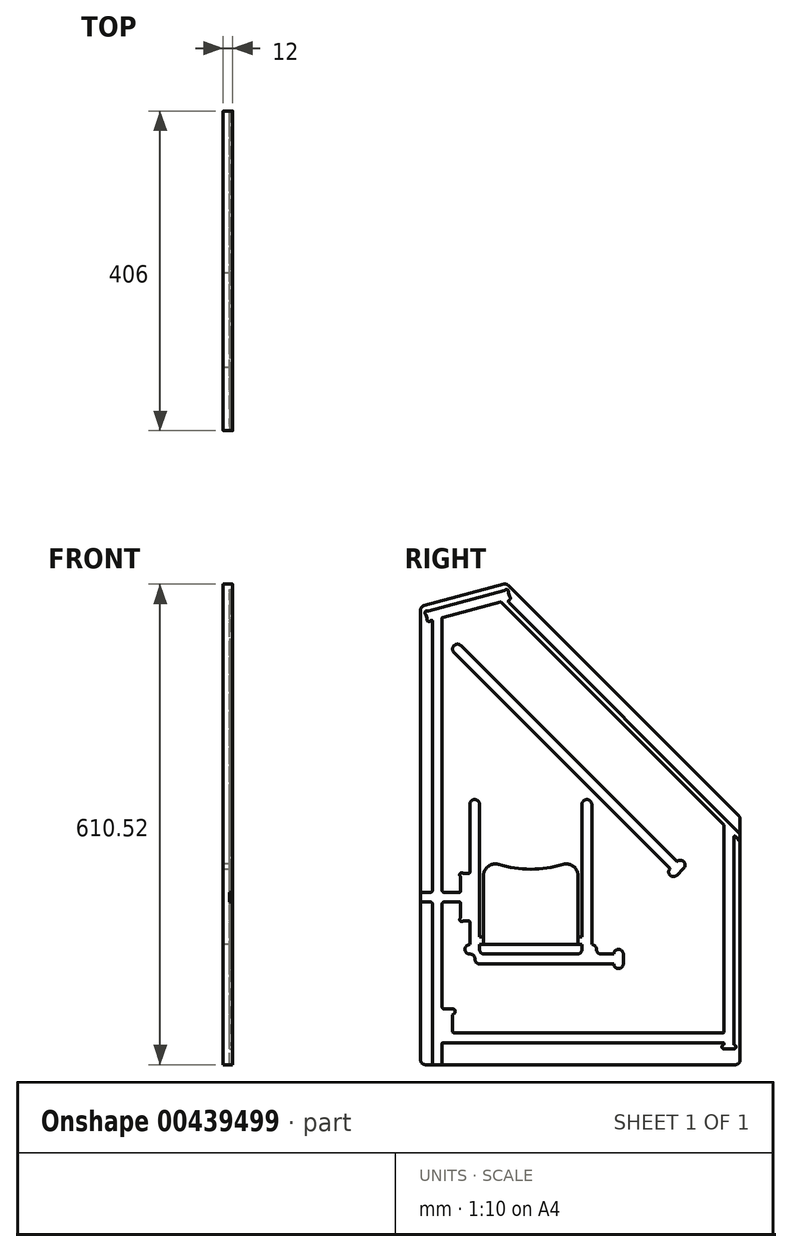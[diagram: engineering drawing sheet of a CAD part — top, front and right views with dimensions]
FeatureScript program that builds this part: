
annotation { "Feature Type Name" : "Feature", "Feature Type Description" : "" }
export const myFeature = defineFeature(function(context is Context, id is Id, definition is map)
    precondition{}
    {
        {
            var Q0;
            Q0=qCreatedBy(makeId("Right.planeOp"),FACE);
            var sketch = newSketch(context, id + "F0", { "sketchPlane" : qUnion([Q0])});
            skLineSegment(sketch, "E0", {"start": v(0, 0) * mm, "end": v(0, 582) * mm});
            skLineSegment(sketch, "E1", {"start": v(0, 582) * mm, "end": v(109.02, 611.21) * mm});
            skLineSegment(sketch, "E2", {"start": v(109.02, 611.21) * mm, "end": v(406, 314.23) * mm});
            skLineSegment(sketch, "E3", {"start": v(406, 314.23) * mm, "end": v(406, 0) * mm});
            skLineSegment(sketch, "E4", {"start": v(406, 0) * mm, "end": v(0, 0) * mm});
            skLineSegment(sketch, "E5", {"start": v(80, 240) * mm, "end": v(80, 152.5) * mm});
            skLineSegment(sketch, "E6", {"start": v(80, 152.5) * mm, "end": v(200, 152.5) * mm});
            skLineSegment(sketch, "E7", {"start": v(200, 152.5) * mm, "end": v(200, 240) * mm});
            skArc(sketch, "E8", {"start": v(200, 240) * mm, "mid": v(193.94, 252.05) * mm, "end": v(180.65, 254.35) * mm});
            skArc(sketch, "E9", {"start": v(99.35, 254.35) * mm, "mid": v(86.06, 252.05) * mm, "end": v(80, 240) * mm});
            skArc(sketch, "E10", {"start": v(99.35, 254.35) * mm, "mid": v(140, 248.32) * mm, "end": v(180.65, 254.35) * mm});
            skSolve(sketch);
        }
        {
            var Q0;
            Q0=qSketchRegion(id+"F0",true);
            extrude(context, id + "F1", {"entities" : qUnion([Q0]), "depth" : 12 * mm, "offsetDistance" : 25.4 * mm});
        }
        {
            var Q0;
            Q0=makeQuery(id+"F1.opExtrude","CAP_FACE",FACE,{"disambiguationData":[OSD([sQuery(id+"F0.wireOp",EDGE,"E0"),sQuery(id+"F0.wireOp",EDGE,"E1"),sQuery(id+"F0.wireOp",EDGE,"E2"),sQuery(id+"F0.wireOp",EDGE,"E3"),sQuery(id+"F0.wireOp",EDGE,"E4")])],"isStart":false});
            var sketch = newSketch(context, id + "F2", { "sketchPlane" : qUnion([Q0])});
            skLineSegment(sketch, "E11", {"start": v(27.5, 0) * mm, "end": v(27.5, 28) * mm});
            skLineSegment(sketch, "E12", {"start": v(27.5, 28) * mm, "end": v(385.5, 28) * mm});
            skLineSegment(sketch, "E13", {"start": v(385.5, 28) * mm, "end": v(385.5, 20) * mm});
            skLineSegment(sketch, "E14", {"start": v(385.5, 20) * mm, "end": v(398, 20) * mm});
            skLineSegment(sketch, "E15", {"start": v(398, 20) * mm, "end": v(398, 291.82) * mm});
            skLineSegment(sketch, "E16", {"start": v(398, 291.82) * mm, "end": v(406, 283.82) * mm});
            skLineSegment(sketch, "E17", {"start": v(410.6, 288.42) * mm, "end": v(109.02, 589.99) * mm});
            skLineSegment(sketch, "E18", {"start": v(101.77, 588.05) * mm, "end": v(385.5, 304.32) * mm});
            skLineSegment(sketch, "E19", {"start": v(385.5, 304.32) * mm, "end": v(385.5, 40.5) * mm});
            skLineSegment(sketch, "E20", {"start": v(385.5, 40.5) * mm, "end": v(40.5, 40.5) * mm});
            skLineSegment(sketch, "E21", {"start": v(27.5, 71) * mm, "end": v(27.5, 128) * mm});
            skLineSegment(sketch, "E22", {"start": v(27.5, 128) * mm, "end": v(257.5, 128) * mm});
            skLineSegment(sketch, "E23", {"start": v(257.5, 128) * mm, "end": v(257.5, 140.5) * mm});
            skLineSegment(sketch, "E24", {"start": v(257.5, 140.5) * mm, "end": v(27.5, 140.5) * mm});
            skLineSegment(sketch, "E25", {"start": v(27.5, 568.15) * mm, "end": v(101.77, 588.05) * mm});
            skLineSegment(sketch, "E26", {"start": v(105.79, 602.06) * mm, "end": v(9.55, 576.28) * mm});
            skLineSegment(sketch, "E27", {"start": v(27.5, 140.5) * mm, "end": v(27.5, 206.5) * mm});
            skLineSegment(sketch, "E28", {"start": v(15, 0) * mm, "end": v(15, 206.5) * mm});
            skLineSegment(sketch, "E29", {"start": v(15, 564.8) * mm, "end": v(12.79, 564.2) * mm});
            skLineSegment(sketch, "E30", {"start": v(9.24, 563.25) * mm, "end": v(8.28, 566.8) * mm, "construction": true});
            skLineSegment(sketch, "E31", {"start": v(51.4, 532.36) * mm, "end": v(334.24, 249.52) * mm});
            skLineSegment(sketch, "E32", {"start": v(334.24, 249.52) * mm, "end": v(325.4, 240.68) * mm});
            skLineSegment(sketch, "E33", {"start": v(325.4, 240.68) * mm, "end": v(42.55, 523.52) * mm});
            skLineSegment(sketch, "E34", {"start": v(406, 283.82) * mm, "end": v(410.6, 288.42) * mm});
            skLineSegment(sketch, "E35", {"start": v(105.79, 602.06) * mm, "end": v(109.02, 589.99) * mm, "construction": true});
            skLineSegment(sketch, "E36", {"start": v(109.02, 589.99) * mm, "end": v(104.43, 585.4) * mm, "construction": true});
            skLineSegment(sketch, "E37", {"start": v(205, 140.5) * mm, "end": v(205, 330.5) * mm});
            skLineSegment(sketch, "E38", {"start": v(75, 330.5) * mm, "end": v(75, 140.5) * mm});
            skLineSegment(sketch, "E39.left", {"start": v(62.5, 330.5) * mm, "end": v(62.5, 243) * mm});
            skLineSegment(sketch, "E39.right", {"start": v(217.5, 330.5) * mm, "end": v(217.5, 140.5) * mm});
            skLineSegment(sketch, "E40", {"start": v(205, 140.5) * mm, "end": v(217.5, 140.5) * mm});
            skLineSegment(sketch, "E41", {"start": v(75, 140.5) * mm, "end": v(62.5, 140.5) * mm});
            skLineSegment(sketch, "E42", {"start": v(75, 140.5) * mm, "end": v(205, 164.5) * mm, "construction": true});
            skLineSegment(sketch, "E43", {"start": v(51.4, 532.36) * mm, "end": v(42.55, 523.52) * mm, "construction": true});
            skArc(sketch, "E44", {"start": v(51.4, 532.36) * mm, "mid": v(42.55, 532.36) * mm, "end": v(42.55, 523.52) * mm});
            skLineSegment(sketch, "E45", {"start": v(62.5, 330.5) * mm, "end": v(75, 330.5) * mm, "construction": true});
            skLineSegment(sketch, "E46", {"start": v(205, 330.5) * mm, "end": v(217.5, 330.5) * mm, "construction": true});
            skArc(sketch, "E47", {"start": v(62.5, 330.5) * mm, "mid": v(68.75, 336.75) * mm, "end": v(75, 330.5) * mm});
            skArc(sketch, "E48", {"start": v(205, 330.5) * mm, "mid": v(211.25, 336.75) * mm, "end": v(217.5, 330.5) * mm});
            skLineSegment(sketch, "E49", {"start": v(27.5, 206.5) * mm, "end": v(50.5, 206.5) * mm});
            skLineSegment(sketch, "E50", {"start": v(50.5, 206.5) * mm, "end": v(50.5, 186.18) * mm});
            skLineSegment(sketch, "E51", {"start": v(50.5, 182.5) * mm, "end": v(54.18, 182.5) * mm, "construction": true});
            skLineSegment(sketch, "E52", {"start": v(50.5, 243) * mm, "end": v(54.18, 243) * mm, "construction": true});
            skLineSegment(sketch, "E53", {"start": v(27.5, 219) * mm, "end": v(50.5, 219) * mm});
            skLineSegment(sketch, "E54", {"start": v(50.5, 219) * mm, "end": v(50.5, 239.32) * mm});
            skLineSegment(sketch, "E55", {"start": v(27.5, 219) * mm, "end": v(27.5, 568.15) * mm});
            skLineSegment(sketch, "E56", {"start": v(62.5, 182.5) * mm, "end": v(62.5, 140.5) * mm});
            skLineSegment(sketch, "E57", {"start": v(15, 219) * mm, "end": v(0, 219) * mm});
            skLineSegment(sketch, "E58", {"start": v(0, 219) * mm, "end": v(0, 206.5) * mm});
            skLineSegment(sketch, "E59", {"start": v(0, 206.5) * mm, "end": v(15, 206.5) * mm});
            skLineSegment(sketch, "E60.trimOffspring", {"start": v(15, 219) * mm, "end": v(15, 564.8) * mm});
            skLineSegment(sketch, "E61", {"start": v(40.5, 40.5) * mm, "end": v(40.5, 64) * mm});
            skLineSegment(sketch, "E62", {"start": v(109.02, 589.99) * mm, "end": v(110.3, 590.33) * mm});
            skLineSegment(sketch, "E63", {"start": v(113.85, 591.28) * mm, "end": v(112.9, 594.84) * mm, "construction": true});
            skLineSegment(sketch, "E64", {"start": v(110.62, 603.36) * mm, "end": v(107.07, 602.4) * mm, "construction": true});
            skLineSegment(sketch, "E65", {"start": v(69, 140.5) * mm, "end": v(69, 128) * mm});
            skLineSegment(sketch, "E66", {"start": v(27.5, 140.5) * mm, "end": v(27.5, 128) * mm});
            skLineSegment(sketch, "E67", {"start": v(40.5, 71) * mm, "end": v(27.5, 71) * mm});
            skArc(sketch, "E68", {"start": v(40.5, 64) * mm, "mid": v(44, 67.5) * mm, "end": v(40.5, 71) * mm});
            skLineSegment(sketch, "E69", {"start": v(40.5, 64) * mm, "end": v(40.5, 71) * mm, "construction": true});
            skArc(sketch, "E70", {"start": v(8.28, 566.8) * mm, "mid": v(9.24, 563.25) * mm, "end": v(12.79, 564.2) * mm});
            skLineSegment(sketch, "E71", {"start": v(12.79, 564.2) * mm, "end": v(9.24, 563.25) * mm, "construction": true});
            skLineSegment(sketch, "E72", {"start": v(8.28, 566.8) * mm, "end": v(6.95, 571.77) * mm});
            skArc(sketch, "E73", {"start": v(9.55, 576.28) * mm, "mid": v(6, 575.33) * mm, "end": v(6.95, 571.77) * mm});
            skLineSegment(sketch, "E74", {"start": v(6.95, 571.77) * mm, "end": v(6, 575.33) * mm, "construction": true});
            skLineSegment(sketch, "E75", {"start": v(9.55, 576.28) * mm, "end": v(6, 575.33) * mm, "construction": true});
            skArc(sketch, "E76", {"start": v(111.57, 599.8) * mm, "mid": v(110.62, 603.36) * mm, "end": v(107.07, 602.4) * mm});
            skLineSegment(sketch, "E77", {"start": v(111.57, 599.8) * mm, "end": v(110.62, 603.36) * mm, "construction": true});
            skLineSegment(sketch, "E78", {"start": v(107.07, 602.4) * mm, "end": v(105.79, 602.06) * mm});
            skArc(sketch, "E79", {"start": v(110.3, 590.33) * mm, "mid": v(113.85, 591.28) * mm, "end": v(112.9, 594.84) * mm});
            skLineSegment(sketch, "E80", {"start": v(112.9, 594.84) * mm, "end": v(111.57, 599.8) * mm});
            skLineSegment(sketch, "E81", {"start": v(110.3, 590.33) * mm, "end": v(113.85, 591.28) * mm, "construction": true});
            skLineSegment(sketch, "E82", {"start": v(112.9, 594.84) * mm, "end": v(110.3, 590.33) * mm, "construction": true});
            skLineSegment(sketch, "E83", {"start": v(54.18, 243) * mm, "end": v(62.5, 243) * mm});
            skLineSegment(sketch, "E84", {"start": v(50.5, 239.32) * mm, "end": v(50.5, 243) * mm, "construction": true});
            skArc(sketch, "E85", {"start": v(54.18, 243) * mm, "mid": v(50.5, 243) * mm, "end": v(50.5, 239.32) * mm});
            skLineSegment(sketch, "E86", {"start": v(54.18, 243) * mm, "end": v(50.5, 239.32) * mm, "construction": true});
            skLineSegment(sketch, "E87", {"start": v(54.18, 182.5) * mm, "end": v(62.5, 182.5) * mm});
            skLineSegment(sketch, "E88", {"start": v(50.5, 186.18) * mm, "end": v(50.5, 182.5) * mm, "construction": true});
            skArc(sketch, "E89", {"start": v(50.5, 186.18) * mm, "mid": v(50.5, 182.5) * mm, "end": v(54.18, 182.5) * mm});
            skLineSegment(sketch, "E90", {"start": v(54.18, 182.5) * mm, "end": v(50.5, 186.18) * mm, "construction": true});
            skSolve(sketch);
        }
        {
            var Q0;
            {var subQ1=sQuery(id+"F2.wireOp",EDGE,"E11");Q0=makeQuery(id+"F2.imprint","IMPRINT",FACE,{"disambiguationData":[TD([[makeQuery(id+"F2.imprint","IMPRINT",EDGE,{"derivedFrom":subQ1}),1.0]])]});}
            var Q1;
            Q1=makeQuery(id+"F2.imprint","IMPRINT",FACE,{"disambiguationData":[TD([[makeQuery(id+"F2.imprint","IMPRINT",EDGE,{"derivedFrom":sQuery(id+"F2.wireOp",EDGE,"E37")}),-1.0]])]});
            var Q2;
            Q2=makeQuery(id+"F2.imprint","IMPRINT",FACE,{"disambiguationData":[TD([[makeQuery(id+"F2.imprint","IMPRINT",EDGE,{"derivedFrom":sQuery(id+"F2.wireOp",EDGE,"E31")}),-1.0]])]});
            var Q3;
            Q3=makeQuery(id+"F2.imprint","IMPRINT",FACE,{"disambiguationData":[TD([[makeQuery(id+"F2.imprint","IMPRINT",EDGE,{"derivedFrom":sQuery(id+"F2.wireOp",EDGE,"E38")}),-1.0]])]});
            var Q4;
            {var subQ0=sQuery(id+"F2.wireOp",EDGE,"E23");Q4=makeQuery(id+"F2.imprint","IMPRINT",FACE,{"disambiguationData":[TD([[makeQuery(id+"F2.imprint","IMPRINT",EDGE,{"derivedFrom":subQ0}),1.0]])]});}
            extrude(context, id + "F3", {"entities" : qUnion([Q0, Q1, Q2, Q3, Q4]), "operationType" : NewBodyOperationType.REMOVE, "oppositeDirection" : true, "depth" : 4 * mm, "offsetDistance" : 25 * mm});
        }
        {
            var Q0;
            {var subQ0=sQuery(id+"F0.wireOp",EDGE,"E0");var subQ1=sQuery(id+"F0.wireOp",EDGE,"E4");var subQ2=sQuery(id+"F0.wireOp",EDGE,"E3");var subQ3=sQuery(id+"F0.wireOp",EDGE,"E1");var subQ4=sQuery(id+"F0.wireOp",EDGE,"E2");Q0=makeQuery(id+"F3.boolean.opBoolean","SPLIT",FACE,{"disambiguationData":[TD([makeQuery(id+"F1.opExtrude","SWEPT_FACE",FACE,{"disambiguationData":[OSD([subQ0])]})])],"derivedFrom":makeQuery(id+"F1.opExtrude","CAP_FACE",FACE,{"disambiguationData":[OSD([subQ0,subQ3,subQ4,subQ2,subQ1])],"isStart":false})});}
            var sketch = newSketch(context, id + "F4", { "sketchPlane" : qUnion([Q0])});
            skArc(sketch, "E91", {"start": v(334.24, 249.52) * mm, "mid": v(334.24, 258) * mm, "end": v(325.75, 258) * mm});
            skArc(sketch, "E92", {"start": v(316.91, 249.16) * mm, "mid": v(316.91, 240.68) * mm, "end": v(325.4, 240.68) * mm});
            skArc(sketch, "E93", {"start": v(257.5, 140.5) * mm, "mid": v(251.5, 146.5) * mm, "end": v(245.5, 140.5) * mm});
            skArc(sketch, "E94", {"start": v(245.5, 128) * mm, "mid": v(251.5, 122) * mm, "end": v(257.5, 128) * mm});
            skArc(sketch, "E95", {"start": v(385.5, 25.2) * mm, "mid": v(382.9, 22.6) * mm, "end": v(385.5, 20) * mm});
            skArc(sketch, "E96", {"start": v(398, 20) * mm, "mid": v(400.6, 22.6) * mm, "end": v(398, 25.2) * mm});
            skLineSegment(sketch, "E97", {"start": v(245.5, 140.5) * mm, "end": v(245.5, 128) * mm});
            skLineSegment(sketch, "E98", {"start": v(257.5, 140.5) * mm, "end": v(257.5, 128) * mm});
            skLineSegment(sketch, "E99", {"start": v(385.5, 20) * mm, "end": v(398, 20) * mm});
            skLineSegment(sketch, "E100", {"start": v(385.5, 25.2) * mm, "end": v(398, 25.2) * mm});
            skLineSegment(sketch, "E101", {"start": v(325.75, 258) * mm, "end": v(316.91, 249.16) * mm});
            skLineSegment(sketch, "E102", {"start": v(325.4, 240.68) * mm, "end": v(334.24, 249.52) * mm});
            skPoint(sketch, "E103", {"position": v(9.55, 576.28) * mm});
            skArc(sketch, "E104", {"start": v(62.5, 152.5) * mm, "mid": v(56.5, 146.5) * mm, "end": v(62.5, 140.5) * mm});
            skLineSegment(sketch, "E105", {"start": v(140, 154.95) * mm, "end": v(140, 133.36) * mm, "construction": true});
            skArc(sketch, "E106.MirrorCS", {"start": v(217.5, 152.5) * mm, "mid": v(223.5, 146.5) * mm, "end": v(217.5, 140.5) * mm});
            skPoint(sketch, "E107", {"position": v(50.5, 219) * mm});
            skPoint(sketch, "E108", {"position": v(50.5, 206.5) * mm});
            skLineSegment(sketch, "E109", {"start": v(62.5, 152.5) * mm, "end": v(62.5, 140.5) * mm});
            skLineSegment(sketch, "E110", {"start": v(217.5, 152.5) * mm, "end": v(217.5, 140.5) * mm});
            skSolve(sketch);
        }
        {
            var Q0;
            {var subQ0=sQuery(id+"F0.wireOp",EDGE,"E8");var subQ1=sQuery(id+"F0.wireOp",EDGE,"E7");var subQ2=sQuery(id+"F0.wireOp",EDGE,"E6");var subQ3=sQuery(id+"F0.wireOp",EDGE,"E5");var subQ4=sQuery(id+"F0.wireOp",EDGE,"E9");var subQ5=sQuery(id+"F0.wireOp",EDGE,"E10");Q0=makeQuery(id+"F3.boolean.opBoolean","SPLIT",FACE,{"disambiguationData":[TD([makeQuery(id+"F1.opExtrude","SWEPT_FACE",FACE,{"disambiguationData":[OSD([subQ3])]})])],"derivedFrom":makeQuery(id+"F1.opExtrude","CAP_FACE",FACE,{"disambiguationData":[OSD([sQuery(id+"F0.wireOp",EDGE,"E0"),sQuery(id+"F0.wireOp",EDGE,"E1"),sQuery(id+"F0.wireOp",EDGE,"E2"),sQuery(id+"F0.wireOp",EDGE,"E3"),sQuery(id+"F0.wireOp",EDGE,"E4"),subQ3,subQ2,subQ1,subQ0,subQ4,subQ5])],"isStart":false})});}
            var sketch = newSketch(context, id + "F5", { "sketchPlane" : qUnion([Q0])});
            skLineSegment(sketch, "E111", {"start": v(76.5, 162.5) * mm, "end": v(80, 162.5) * mm});
            skLineSegment(sketch, "E112", {"start": v(80, 162.5) * mm, "end": v(75, 162.5) * mm});
            skLineSegment(sketch, "E113", {"start": v(80, 152.5) * mm, "end": v(75, 152.5) * mm});
            skLineSegment(sketch, "E114", {"start": v(75, 152.5) * mm, "end": v(75, 162.5) * mm});
            skLineSegment(sketch, "E115", {"start": v(80, 162.5) * mm, "end": v(80, 152.5) * mm});
            skLineSegment(sketch, "E116", {"start": v(75, 162.5) * mm, "end": v(75, 152.5) * mm});
            skLineSegment(sketch, "E117", {"start": v(200, 162.5) * mm, "end": v(200, 152.5) * mm});
            skLineSegment(sketch, "E118", {"start": v(200, 152.5) * mm, "end": v(205, 152.5) * mm});
            skLineSegment(sketch, "E119", {"start": v(205, 152.5) * mm, "end": v(205, 162.5) * mm});
            skLineSegment(sketch, "E120", {"start": v(205, 162.5) * mm, "end": v(200, 162.5) * mm});
            skSolve(sketch);
        }
        {
            var Q0;
            Q0 = qSketchRegion(id + "F5", true);
            extrude(context, id + "F6", {"entities" : qUnion([Q0]), "operationType" : NewBodyOperationType.REMOVE, "oppositeDirection" : true, "depth" : 4 * mm, "offsetDistance" : 25 * mm});
        }
        {
            var Q0;
            Q0=qSketchRegion(id+"F4",true);
            var Q1;
            {var subQ0=sQuery(id+"F4.wireOp",EDGE,"urzTXQ1m-be9f-dkH4-n3dN-gv34R3q4TUyH");var subQ1=makeQuery(id+"F3.boolean.opBoolean","COPY",EDGE,{"derivedFrom":makeQuery(id+"F3.opExtrude","CAP_EDGE",EDGE,{"disambiguationData":[OSD([sQuery(id+"F2.wireOp",EDGE,"E26")])],"isStart":true})});var subQ3=makeQuery(id+"F4.imprint","INTERSECT",VERTEX,{"derivedFrom":[subQ1,subQ0]});Q1=makeQuery(id+"F4.imprint","IMPRINT",FACE,{"disambiguationData":[TD([[makeQuery(id+"F4.imprint","IMPRINT",EDGE,{"disambiguationData":[TD([[subQ3,-1.0]])],"derivedFrom":subQ0}),1.0]])]});}
            var Q2;
            {var subQ0=sQuery(id+"F4.wireOp",EDGE,"xMWXty8K-vTmh-I9ST-5zzS-5fXN0JypUEpW");var subQ1=makeQuery(id+"F3.boolean.opBoolean","COPY",EDGE,{"derivedFrom":makeQuery(id+"F3.opExtrude","CAP_EDGE",EDGE,{"disambiguationData":[OSD([sQuery(id+"F2.wireOp",EDGE,"E30")])],"isStart":true})});var subQ3=makeQuery(id+"F4.imprint","INTERSECT",VERTEX,{"derivedFrom":[subQ1,subQ0]});Q2=makeQuery(id+"F4.imprint","IMPRINT",FACE,{"disambiguationData":[TD([[makeQuery(id+"F4.imprint","IMPRINT",EDGE,{"disambiguationData":[TD([[subQ3,-1.0]])],"derivedFrom":subQ0}),1.0]])]});}
            var Q3;
            {var subQ0=sQuery(id+"F4.wireOp",EDGE,"xMWXty8K-vTmh-I9ST-5zzS-5fXN0JypUEpW");var subQ1=makeQuery(id+"F3.boolean.opBoolean","COPY",EDGE,{"derivedFrom":makeQuery(id+"F3.opExtrude","CAP_EDGE",EDGE,{"disambiguationData":[OSD([sQuery(id+"F2.wireOp",EDGE,"E29")])],"isStart":true})});var subQ3=makeQuery(id+"F4.imprint","INTERSECT",VERTEX,{"derivedFrom":[subQ1,subQ0]});Q3=makeQuery(id+"F4.imprint","IMPRINT",FACE,{"disambiguationData":[TD([[makeQuery(id+"F4.imprint","IMPRINT",EDGE,{"disambiguationData":[TD([[subQ3,1.0]])],"derivedFrom":subQ0}),1.0]])]});}
            var Q4;
            {var subQ0=sQuery(id+"F4.wireOp",EDGE,"urzTXQ1m-be9f-dkH4-n3dN-gv34R3q4TUyH");var subQ1=makeQuery(id+"F3.boolean.opBoolean","COPY",EDGE,{"derivedFrom":makeQuery(id+"F3.opExtrude","CAP_EDGE",EDGE,{"disambiguationData":[OSD([sQuery(id+"F2.wireOp",EDGE,"E30")])],"isStart":true})});var subQ3=makeQuery(id+"F4.imprint","INTERSECT",VERTEX,{"derivedFrom":[subQ1,subQ0]});Q4=makeQuery(id+"F4.imprint","IMPRINT",FACE,{"disambiguationData":[TD([[makeQuery(id+"F4.imprint","IMPRINT",EDGE,{"disambiguationData":[TD([[subQ3,1.0]])],"derivedFrom":subQ0}),1.0]])]});}
            var Q5;
            {var subQ0=sQuery(id+"F4.wireOp",EDGE,"6hAEF9lr-ykpB-nCDN-qJi7-kB8WBNifAdNi");Q5=makeQuery(id+"F4.imprint","IMPRINT",FACE,{"disambiguationData":[TD([[makeQuery(id+"F4.imprint","IMPRINT",EDGE,{"derivedFrom":subQ0}),1.0]])]});}
            extrude(context, id + "F7", {"entities" : qUnion([Q0, Q1, Q2, Q3, Q4, Q5]), "operationType" : NewBodyOperationType.REMOVE, "oppositeDirection" : true, "depth" : 4 * mm, "offsetDistance" : 25 * mm});
        }
        {
            var Q0;
            Q0=makeQuery(id+"F7.boolean.opBoolean","COPY",EDGE,{"derivedFrom":makeQuery(id+"F7.opExtrude","SWEPT_EDGE",EDGE,{"disambiguationData":[OSD([sQuery(id+"F4.wireOp",EDGE,"E96"),sQuery(id+"F4.wireOp",EDGE,"E100")])]})});
            var Q1;
            Q1=makeQuery(id+"F7.boolean.opBoolean","COPY",EDGE,{"derivedFrom":makeQuery(id+"F7.opExtrude","SWEPT_EDGE",EDGE,{"disambiguationData":[OSD([sQuery(id+"F4.wireOp",EDGE,"E95"),sQuery(id+"F4.wireOp",EDGE,"E100")])]})});
            var Q2;
            Q2=makeQuery(id+"F3.boolean.opBoolean","COPY",EDGE,{"derivedFrom":makeQuery(id+"F3.opExtrude","SWEPT_EDGE",EDGE,{"disambiguationData":[OSD([sQuery(id+"F2.wireOp",EDGE,"E12"),sQuery(id+"F2.wireOp",EDGE,"E13")])]})});
            var Q3;
            Q3=makeQuery(id+"F7.boolean.opBoolean","COPY",EDGE,{"derivedFrom":makeQuery(id+"F7.opExtrude","SWEPT_EDGE",EDGE,{"disambiguationData":[OSD([sQuery(id+"F4.wireOp",EDGE,"E96"),sQuery(id+"F4.wireOp",EDGE,"E99")])]})});
            var Q4;
            Q4=makeQuery(id+"F3.boolean.opBoolean","COPY",EDGE,{"derivedFrom":makeQuery(id+"F3.opExtrude","SWEPT_EDGE",EDGE,{"disambiguationData":[OSD([sQuery(id+"F2.wireOp",EDGE,"E15"),sQuery(id+"F2.wireOp",EDGE,"E16")])]})});
            var Q5;
            Q5=makeQuery(id+"F3.boolean.opBoolean","COPY",EDGE,{"derivedFrom":makeQuery(id+"F3.opExtrude","SWEPT_EDGE",EDGE,{"disambiguationData":[OSD([sQuery(id+"F0.wireOp",EDGE,"E3"),sQuery(id+"F2.wireOp",EDGE,"E17")])]})});
            var Q6;
            Q6=makeQuery(id+"F3.boolean.opBoolean","COPY",EDGE,{"derivedFrom":makeQuery(id+"F3.opExtrude","SWEPT_EDGE",EDGE,{"disambiguationData":[OSD([sQuery(id+"F0.wireOp",EDGE,"E3"),sQuery(id+"F2.wireOp",EDGE,"E16"),sQuery(id+"F2.wireOp",EDGE,"E34")])]})});
            var Q7;
            Q7=makeQuery(id+"F3.boolean.opBoolean","COPY",EDGE,{"derivedFrom":makeQuery(id+"F3.opExtrude","SWEPT_EDGE",EDGE,{"disambiguationData":[OSD([sQuery(id+"F2.wireOp",EDGE,"E18"),sQuery(id+"F2.wireOp",EDGE,"E19")])]})});
            var Q8;
            Q8=makeQuery(id+"F3.boolean.opBoolean","COPY",EDGE,{"derivedFrom":makeQuery(id+"F3.opExtrude","SWEPT_EDGE",EDGE,{"disambiguationData":[OSD([sQuery(id+"F2.wireOp",EDGE,"E18"),sQuery(id+"F2.wireOp",EDGE,"e1bb6627-fa48-4d6d-a6f5-fe5e6ec525b7")])]})});
            var Q9;
            Q9=makeQuery(id+"F7.boolean.opBoolean","COPY",EDGE,{"derivedFrom":makeQuery(id+"F7.opExtrude","SWEPT_EDGE",EDGE,{"disambiguationData":[OSD([sQuery(id+"F2.wireOp",EDGE,"E26"),sQuery(id+"F4.wireOp",EDGE,"6hAEF9lr-ykpB-nCDN-qJi7-kB8WBNifAdNi")])]})});
            var Q10;
            {var subQ0=sQuery(id+"F2.wireOp",EDGE,"E35");var subQ1=sQuery(id+"F2.wireOp",EDGE,"E26");Q10=makeQuery(id+"F7.boolean.opBoolean","MERGE",EDGE,{"derivedFrom":[makeQuery(id+"F3.boolean.opBoolean","COPY",EDGE,{"derivedFrom":makeQuery(id+"F3.opExtrude","SWEPT_EDGE",EDGE,{"disambiguationData":[OSD([subQ1,subQ0])]})})],"fromTools":[makeQuery(id+"F7.opExtrude","SWEPT_EDGE",EDGE,{"disambiguationData":[OSD([subQ1,subQ0,sQuery(id+"F4.wireOp",EDGE,"6hAEF9lr-ykpB-nCDN-qJi7-kB8WBNifAdNi")])]})]});}
            var Q11;
            Q11=makeQuery(id+"F3.boolean.opBoolean","COPY",EDGE,{"derivedFrom":makeQuery(id+"F3.opExtrude","SWEPT_EDGE",EDGE,{"disambiguationData":[OSD([sQuery(id+"F2.wireOp",EDGE,"E17"),sQuery(id+"F2.wireOp",EDGE,"E35")])]})});
            var Q12;
            Q12=makeQuery(id+"F7.boolean.opBoolean","COPY",EDGE,{"derivedFrom":makeQuery(id+"F7.opExtrude","SWEPT_EDGE",EDGE,{"disambiguationData":[OSD([sQuery(id+"F2.wireOp",EDGE,"E30"),sQuery(id+"F4.wireOp",EDGE,"urzTXQ1m-be9f-dkH4-n3dN-gv34R3q4TUyH")])]})});
            var Q13;
            Q13=makeQuery(id+"F7.boolean.opBoolean","COPY",EDGE,{"derivedFrom":makeQuery(id+"F7.opExtrude","SWEPT_EDGE",EDGE,{"disambiguationData":[OSD([sQuery(id+"F2.wireOp",EDGE,"E30"),sQuery(id+"F4.wireOp",EDGE,"xMWXty8K-vTmh-I9ST-5zzS-5fXN0JypUEpW")])]})});
            var Q14;
            Q14=makeQuery(id+"F7.boolean.opBoolean","COPY",EDGE,{"derivedFrom":makeQuery(id+"F7.opExtrude","SWEPT_EDGE",EDGE,{"disambiguationData":[OSD([sQuery(id+"F2.wireOp",EDGE,"E29"),sQuery(id+"F4.wireOp",EDGE,"xMWXty8K-vTmh-I9ST-5zzS-5fXN0JypUEpW")])]})});
            var Q15;
            Q15=makeQuery(id+"F7.boolean.opBoolean","COPY",EDGE,{"derivedFrom":makeQuery(id+"F7.opExtrude","SWEPT_EDGE",EDGE,{"disambiguationData":[OSD([sQuery(id+"F2.wireOp",EDGE,"E26"),sQuery(id+"F4.wireOp",EDGE,"urzTXQ1m-be9f-dkH4-n3dN-gv34R3q4TUyH")])]})});
            var Q16;
            Q16=makeQuery(id+"F7.boolean.opBoolean","COPY",EDGE,{"derivedFrom":makeQuery(id+"F7.opExtrude","SWEPT_EDGE",EDGE,{"disambiguationData":[OSD([sQuery(id+"F2.wireOp",EDGE,"E35"),sQuery(id+"F4.wireOp",EDGE,"6hAEF9lr-ykpB-nCDN-qJi7-kB8WBNifAdNi")])]})});
            var Q17;
            Q17=makeQuery(id+"F7.boolean.opBoolean","COPY",EDGE,{"derivedFrom":makeQuery(id+"F7.opExtrude","SWEPT_EDGE",EDGE,{"disambiguationData":[OSD([sQuery(id+"F4.wireOp",EDGE,"CceDpIPY-w2kd-guYH-PqJx-6DTV4oBaQIcy"),sQuery(id+"F4.wireOp",EDGE,"fr93pYOe-dN8n-CsNu-HKSh-kEzRfjo7Obc8")])]})});
            var Q18;
            Q18=makeQuery(id+"F7.boolean.opBoolean","COPY",EDGE,{"derivedFrom":makeQuery(id+"F7.opExtrude","SWEPT_EDGE",EDGE,{"disambiguationData":[OSD([sQuery(id+"F4.wireOp",EDGE,"CceDpIPY-w2kd-guYH-PqJx-6DTV4oBaQIcy"),sQuery(id+"F4.wireOp",EDGE,"wFOvSmpO-cCdS-8Kfr-Gnzh-tl23NCxo1hq1")])]})});
            var Q19;
            Q19=makeQuery(id+"F7.boolean.opBoolean","COPY",EDGE,{"derivedFrom":makeQuery(id+"F7.opExtrude","SWEPT_EDGE",EDGE,{"disambiguationData":[OSD([sQuery(id+"F4.wireOp",EDGE,"d346fed3-e3b7-45c1-9c38-52b7115230742.MirrorCS"),sQuery(id+"F4.wireOp",EDGE,"d346fed3-e3b7-45c1-9c38-52b7115230743.MirrorCS")])]})});
            var Q20;
            Q20=makeQuery(id+"F7.boolean.opBoolean","COPY",EDGE,{"derivedFrom":makeQuery(id+"F7.opExtrude","SWEPT_EDGE",EDGE,{"disambiguationData":[OSD([sQuery(id+"F4.wireOp",EDGE,"d346fed3-e3b7-45c1-9c38-52b7115230741.MirrorCS"),sQuery(id+"F4.wireOp",EDGE,"d346fed3-e3b7-45c1-9c38-52b7115230743.MirrorCS")])]})});
            var Q21;
            Q21=makeQuery(id+"F3.boolean.opBoolean","COPY",EDGE,{"derivedFrom":makeQuery(id+"F3.opExtrude","SWEPT_EDGE",EDGE,{"disambiguationData":[OSD([sQuery(id+"F2.wireOp",EDGE,"E29"),sQuery(id+"F2.wireOp",EDGE,"E60.trimOffspring")])]})});
            fillet(context, id + "F8", {"entities" : qUnion([Q0, Q1, Q2, Q3, Q4, Q5, Q6, Q7, Q8, Q9, Q10, Q11, Q12, Q13, Q14, Q15, Q16, Q17, Q18, Q19, Q20, Q21]), "radius" : 1 * mm, "tangentPropagation" : true, "allowEdgeOverflow" : false});
        }
        {
            var Q0;
            Q0=makeQuery(id+"F3.boolean.opBoolean","COPY",EDGE,{"derivedFrom":makeQuery(id+"F3.opExtrude","SWEPT_EDGE",EDGE,{"disambiguationData":[OSD([sQuery(id+"F2.wireOp",EDGE,"E21"),sQuery(id+"F2.wireOp",EDGE,"npoSXuDm-Eoiq-LSfY-cZaE-gJeQPJGgDAUd")])]})});
            var Q1;
            Q1=makeQuery(id+"F3.boolean.opBoolean","COPY",EDGE,{"derivedFrom":makeQuery(id+"F3.opExtrude","SWEPT_EDGE",EDGE,{"disambiguationData":[OSD([sQuery(id+"F0.wireOp",EDGE,"E4"),sQuery(id+"F2.wireOp",EDGE,"E11")])]})});
            var Q2;
            Q2=makeQuery(id+"F3.boolean.opBoolean","COPY",EDGE,{"derivedFrom":makeQuery(id+"F3.opExtrude","SWEPT_EDGE",EDGE,{"disambiguationData":[OSD([sQuery(id+"F0.wireOp",EDGE,"E4"),sQuery(id+"F2.wireOp",EDGE,"E28")])]})});
            var Q3;
            Q3=makeQuery(id+"F3.boolean.opBoolean","COPY",EDGE,{"derivedFrom":makeQuery(id+"F3.opExtrude","SWEPT_EDGE",EDGE,{"disambiguationData":[OSD([sQuery(id+"F2.wireOp",EDGE,"E53"),sQuery(id+"F2.wireOp",EDGE,"E55")])]})});
            var Q4;
            Q4=makeQuery(id+"F3.boolean.opBoolean","COPY",EDGE,{"derivedFrom":makeQuery(id+"F3.opExtrude","SWEPT_EDGE",EDGE,{"disambiguationData":[OSD([sQuery(id+"F2.wireOp",EDGE,"E27"),sQuery(id+"F2.wireOp",EDGE,"E49")])]})});
            var Q5;
            Q5=makeQuery(id+"F3.boolean.opBoolean","COPY",EDGE,{"derivedFrom":makeQuery(id+"F3.opExtrude","SWEPT_EDGE",EDGE,{"disambiguationData":[OSD([sQuery(id+"F2.wireOp",EDGE,"E57"),sQuery(id+"F2.wireOp",EDGE,"E60.trimOffspring")])]})});
            var Q6;
            Q6=makeQuery(id+"F3.boolean.opBoolean","COPY",EDGE,{"derivedFrom":makeQuery(id+"F3.opExtrude","SWEPT_EDGE",EDGE,{"disambiguationData":[OSD([sQuery(id+"F0.wireOp",EDGE,"E0"),sQuery(id+"F2.wireOp",EDGE,"E57"),sQuery(id+"F2.wireOp",EDGE,"E58")])]})});
            var Q7;
            Q7=makeQuery(id+"F3.boolean.opBoolean","COPY",EDGE,{"derivedFrom":makeQuery(id+"F3.opExtrude","SWEPT_EDGE",EDGE,{"disambiguationData":[OSD([sQuery(id+"F0.wireOp",EDGE,"E0"),sQuery(id+"F2.wireOp",EDGE,"E58"),sQuery(id+"F2.wireOp",EDGE,"E59")])]})});
            var Q8;
            Q8=makeQuery(id+"F3.boolean.opBoolean","COPY",EDGE,{"derivedFrom":makeQuery(id+"F3.opExtrude","SWEPT_EDGE",EDGE,{"disambiguationData":[OSD([sQuery(id+"F2.wireOp",EDGE,"E28"),sQuery(id+"F2.wireOp",EDGE,"E59")])]})});
            var Q9;
            Q9=makeQuery(id+"F3.boolean.opBoolean","COPY",EDGE,{"derivedFrom":makeQuery(id+"F3.opExtrude","SWEPT_EDGE",EDGE,{"disambiguationData":[OSD([sQuery(id+"F0.wireOp",EDGE,"VAvj4DLE-OLLv-OTpa-dZqd-xAeIvvhF6Rpz"),sQuery(id+"F2.wireOp",EDGE,"szvPPvtx-yQEH-X6NK-ylIl-m7RT24W2dFBS"),sQuery(id+"F2.wireOp",EDGE,"96wn82cF-uFPj-i8m8-NWIa-4QTA4rWPUXw8")])]})});
            var Q10;
            Q10=makeQuery(id+"F3.boolean.opBoolean","COPY",EDGE,{"derivedFrom":makeQuery(id+"F3.opExtrude","SWEPT_EDGE",EDGE,{"disambiguationData":[OSD([sQuery(id+"F0.wireOp",EDGE,"VAvj4DLE-OLLv-OTpa-dZqd-xAeIvvhF6Rpz"),sQuery(id+"F2.wireOp",EDGE,"kYrd408Q-q4gh-1TsQ-sOge-Qtq1zwTrqfUa"),sQuery(id+"F2.wireOp",EDGE,"96wn82cF-uFPj-i8m8-NWIa-4QTA4rWPUXw8")])]})});
            var Q11;
            Q11=makeQuery(id+"F3.boolean.opBoolean","COPY",EDGE,{"derivedFrom":makeQuery(id+"F3.opExtrude","SWEPT_EDGE",EDGE,{"disambiguationData":[OSD([sQuery(id+"F2.wireOp",EDGE,"E61"),sQuery(id+"F2.wireOp",EDGE,"E68")])]})});
            var Q12;
            Q12=makeQuery(id+"F3.boolean.opBoolean","COPY",EDGE,{"derivedFrom":makeQuery(id+"F3.opExtrude","SWEPT_EDGE",EDGE,{"disambiguationData":[OSD([sQuery(id+"F2.wireOp",EDGE,"E20"),sQuery(id+"F2.wireOp",EDGE,"E61")])]})});
            var Q13;
            Q13=makeQuery(id+"F8.opFillet","BLEND_EDGE",EDGE,{"blendedFrom":[makeQuery(id+"F3.boolean.opBoolean","COPY",EDGE,{"derivedFrom":makeQuery(id+"F3.opExtrude","SWEPT_EDGE",EDGE,{"disambiguationData":[OSD([sQuery(id+"F2.wireOp",EDGE,"E17"),sQuery(id+"F2.wireOp",EDGE,"E62")])]})}),makeQuery(id+"F3.boolean.opBoolean","COPY",FACE,{"derivedFrom":makeQuery(id+"F3.opExtrude","SWEPT_FACE",FACE,{"disambiguationData":[OSD([sQuery(id+"F2.wireOp",EDGE,"E79")])]})})],"blendedInto":[makeQuery(id+"F3.boolean.opBoolean","COPY",FACE,{"derivedFrom":makeQuery(id+"F3.opExtrude","SWEPT_FACE",FACE,{"disambiguationData":[OSD([sQuery(id+"F2.wireOp",EDGE,"E79")])]})})]});
            var Q14;
            Q14=makeQuery(id+"F3.boolean.opBoolean","COPY",EDGE,{"derivedFrom":makeQuery(id+"F3.opExtrude","SWEPT_EDGE",EDGE,{"disambiguationData":[OSD([sQuery(id+"F2.wireOp",EDGE,"E79"),sQuery(id+"F2.wireOp",EDGE,"E80")])]})});
            var Q15;
            Q15=makeQuery(id+"F3.boolean.opBoolean","COPY",EDGE,{"derivedFrom":makeQuery(id+"F3.opExtrude","SWEPT_EDGE",EDGE,{"disambiguationData":[OSD([sQuery(id+"F2.wireOp",EDGE,"E76"),sQuery(id+"F2.wireOp",EDGE,"E80")])]})});
            var Q16;
            Q16=makeQuery(id+"F3.boolean.opBoolean","COPY",EDGE,{"derivedFrom":makeQuery(id+"F3.opExtrude","SWEPT_EDGE",EDGE,{"disambiguationData":[OSD([sQuery(id+"F2.wireOp",EDGE,"E76"),sQuery(id+"F2.wireOp",EDGE,"E78")])]})});
            var Q17;
            Q17=makeQuery(id+"F3.boolean.opBoolean","COPY",EDGE,{"derivedFrom":makeQuery(id+"F3.opExtrude","SWEPT_EDGE",EDGE,{"disambiguationData":[OSD([sQuery(id+"F2.wireOp",EDGE,"E26"),sQuery(id+"F2.wireOp",EDGE,"E73")])]})});
            var Q18;
            Q18=makeQuery(id+"F3.boolean.opBoolean","COPY",EDGE,{"derivedFrom":makeQuery(id+"F3.opExtrude","SWEPT_EDGE",EDGE,{"disambiguationData":[OSD([sQuery(id+"F2.wireOp",EDGE,"E72"),sQuery(id+"F2.wireOp",EDGE,"E73")])]})});
            var Q19;
            Q19=makeQuery(id+"F3.boolean.opBoolean","COPY",EDGE,{"derivedFrom":makeQuery(id+"F3.opExtrude","SWEPT_EDGE",EDGE,{"disambiguationData":[OSD([sQuery(id+"F2.wireOp",EDGE,"E70"),sQuery(id+"F2.wireOp",EDGE,"E72")])]})});
            var Q20;
            Q20=makeQuery(id+"F3.boolean.opBoolean","COPY",EDGE,{"derivedFrom":makeQuery(id+"F3.opExtrude","SWEPT_EDGE",EDGE,{"disambiguationData":[OSD([sQuery(id+"F2.wireOp",EDGE,"E29"),sQuery(id+"F2.wireOp",EDGE,"E70")])]})});
            var Q21;
            Q21=makeQuery(id+"F6.boolean.opBoolean","COPY",EDGE,{"derivedFrom":makeQuery(id+"F6.opExtrude","SWEPT_EDGE",EDGE,{"disambiguationData":[OSD([sQuery(id+"F0.wireOp",EDGE,"E6"),sQuery(id+"F5.wireOp",EDGE,"385b752d-af89-4aa4-a548-ba333403f6dc"),sQuery(id+"F5.wireOp",EDGE,"ZSCoYtNK-O37y-rSft-lgkM-Z8ndqeqG6MgS")])]})});
            var Q22;
            Q22=makeQuery(id+"F6.boolean.opBoolean","COPY",EDGE,{"derivedFrom":makeQuery(id+"F6.opExtrude","SWEPT_EDGE",EDGE,{"disambiguationData":[OSD([sQuery(id+"F0.wireOp",EDGE,"E6"),sQuery(id+"F5.wireOp",EDGE,"0afee4d4-881f-4a1d-b8ed-13ce27edee123.MirrorCS"),sQuery(id+"F5.wireOp",EDGE,"ZSCoYtNK-O37y-rSft-lgkM-Z8ndqeqG6MgS")])]})});
            fillet(context, id + "F9", {"entities" : qUnion([Q0, Q1, Q2, Q3, Q4, Q5, Q6, Q7, Q8, Q9, Q10, Q11, Q12, Q13, Q14, Q15, Q16, Q17, Q18, Q19, Q20, Q21, Q22]), "radius" : 2 * mm, "tangentPropagation" : true, "defaultsChanged" : false, "vertexSettings" : [], "allowEdgeOverflow" : false});
        }
        {
            var Q0;
            Q0=makeQuery(id+"F1.opExtrude","SWEPT_EDGE",EDGE,{"disambiguationData":[OSD([sQuery(id+"F0.wireOp",EDGE,"E0"),sQuery(id+"F0.wireOp",EDGE,"E4")])]});
            var Q1;
            Q1=makeQuery(id+"F1.opExtrude","SWEPT_EDGE",EDGE,{"disambiguationData":[OSD([sQuery(id+"F0.wireOp",EDGE,"E3"),sQuery(id+"F0.wireOp",EDGE,"E4")])]});
            var Q2;
            Q2=makeQuery(id+"F1.opExtrude","SWEPT_EDGE",EDGE,{"disambiguationData":[OSD([sQuery(id+"F0.wireOp",EDGE,"E2"),sQuery(id+"F0.wireOp",EDGE,"E3")])]});
            var Q3;
            Q3=makeQuery(id+"F1.opExtrude","SWEPT_EDGE",EDGE,{"disambiguationData":[OSD([sQuery(id+"F0.wireOp",EDGE,"E1"),sQuery(id+"F0.wireOp",EDGE,"E2")])]});
            var Q4;
            Q4=makeQuery(id+"F1.opExtrude","SWEPT_EDGE",EDGE,{"disambiguationData":[OSD([sQuery(id+"F0.wireOp",EDGE,"E0"),sQuery(id+"F0.wireOp",EDGE,"E1")])]});
            var Q5;
            Q5=makeQuery(id+"F3.boolean.opBoolean","COPY",EDGE,{"derivedFrom":makeQuery(id+"F3.opExtrude","SWEPT_EDGE",EDGE,{"disambiguationData":[OSD([sQuery(id+"F2.wireOp",EDGE,"E24"),sQuery(id+"F2.wireOp",EDGE,"E27")])]})});
            var Q6;
            Q6=makeQuery(id+"F3.boolean.opBoolean","COPY",EDGE,{"derivedFrom":makeQuery(id+"F3.opExtrude","SWEPT_EDGE",EDGE,{"disambiguationData":[OSD([sQuery(id+"F2.wireOp",EDGE,"E21"),sQuery(id+"F2.wireOp",EDGE,"E22")])]})});
            var Q7;
            Q7=makeQuery(id+"F1.opExtrude","SWEPT_EDGE",EDGE,{"disambiguationData":[OSD([sQuery(id+"F0.wireOp",EDGE,"R3NtdDFS-bnrZ-jgbp-EYRp-KaoF9L5EDQX5"),sQuery(id+"F0.wireOp",EDGE,"VAvj4DLE-OLLv-OTpa-dZqd-xAeIvvhF6Rpz")])]});
            var Q8;
            Q8=makeQuery(id+"F1.opExtrude","SWEPT_EDGE",EDGE,{"disambiguationData":[OSD([sQuery(id+"F0.wireOp",EDGE,"cF9Nu0SH-aran-s4be-sOBd-E3YfxXrbXWl8"),sQuery(id+"F0.wireOp",EDGE,"cyWnLqfm-qHlC-bZCh-tJEp-L87q5ZNfodfB")])]});
            fillet(context, id + "F10", {"entities" : qUnion([Q0, Q1, Q2, Q3, Q4, Q5, Q6, Q7, Q8]), "radius" : 6 * mm, "tangentPropagation" : true, "defaultsChanged" : false, "vertexSettings" : [], "allowEdgeOverflow" : false});
        }
        {
            var Q0;
            Q0=makeQuery(id+"F3.boolean.opBoolean","COPY",EDGE,{"derivedFrom":makeQuery(id+"F3.opExtrude","SWEPT_EDGE",EDGE,{"disambiguationData":[OSD([sQuery(id+"F2.wireOp",EDGE,"E25"),sQuery(id+"F2.wireOp",EDGE,"E55")])]})});
            var Q1;
            Q1=makeQuery(id+"F7.boolean.opBoolean","COPY",EDGE,{"derivedFrom":makeQuery(id+"F7.opExtrude","SWEPT_EDGE",EDGE,{"disambiguationData":[OSD([sQuery(id+"F4.wireOp",EDGE,"E104"),sQuery(id+"F4.wireOp",EDGE,"wFOvSmpO-cCdS-8Kfr-Gnzh-tl23NCxo1hq1")])]})});
            var Q2;
            Q2=makeQuery(id+"F7.boolean.opBoolean","COPY",EDGE,{"derivedFrom":makeQuery(id+"F7.opExtrude","SWEPT_EDGE",EDGE,{"disambiguationData":[OSD([sQuery(id+"F4.wireOp",EDGE,"E106.MirrorCS"),sQuery(id+"F4.wireOp",EDGE,"d346fed3-e3b7-45c1-9c38-52b7115230742.MirrorCS")])]})});
            var Q3;
            Q3=makeQuery(id+"F3.boolean.opBoolean","COPY",EDGE,{"derivedFrom":makeQuery(id+"F3.opExtrude","SWEPT_EDGE",EDGE,{"disambiguationData":[OSD([sQuery(id+"F2.wireOp",EDGE,"E19"),sQuery(id+"F2.wireOp",EDGE,"E20")])]})});
            var Q4;
            Q4=makeQuery(id+"F3.boolean.opBoolean","COPY",EDGE,{"derivedFrom":makeQuery(id+"F3.opExtrude","SWEPT_EDGE",EDGE,{"disambiguationData":[OSD([sQuery(id+"F2.wireOp",EDGE,"E20"),sQuery(id+"F2.wireOp",EDGE,"E61")])]})});
            var Q5;
            Q5=makeQuery(id+"F3.boolean.opBoolean","COPY",EDGE,{"derivedFrom":makeQuery(id+"F3.opExtrude","SWEPT_EDGE",EDGE,{"disambiguationData":[OSD([sQuery(id+"F2.wireOp",EDGE,"E11"),sQuery(id+"F2.wireOp",EDGE,"E12")])]})});
            var Q6;
            Q6=makeQuery(id+"F7.boolean.opBoolean","COPY",EDGE,{"derivedFrom":makeQuery(id+"F7.opExtrude","SWEPT_EDGE",EDGE,{"disambiguationData":[OSD([sQuery(id+"F4.wireOp",EDGE,"E93"),sQuery(id+"F4.wireOp",EDGE,"E97")])]})});
            var Q7;
            Q7=makeQuery(id+"F7.boolean.opBoolean","COPY",EDGE,{"derivedFrom":makeQuery(id+"F7.opExtrude","SWEPT_EDGE",EDGE,{"disambiguationData":[OSD([sQuery(id+"F4.wireOp",EDGE,"E94"),sQuery(id+"F4.wireOp",EDGE,"E97")])]})});
            var Q8;
            Q8=makeQuery(id+"F3.boolean.opBoolean","COPY",EDGE,{"derivedFrom":makeQuery(id+"F3.opExtrude","SWEPT_EDGE",EDGE,{"disambiguationData":[OSD([sQuery(id+"F2.wireOp",EDGE,"E51"),sQuery(id+"F2.wireOp",EDGE,"E56")])]})});
            var Q9;
            Q9=makeQuery(id+"F3.boolean.opBoolean","COPY",EDGE,{"derivedFrom":makeQuery(id+"F3.opExtrude","SWEPT_EDGE",EDGE,{"disambiguationData":[OSD([sQuery(id+"F2.wireOp",EDGE,"E49"),sQuery(id+"F2.wireOp",EDGE,"E50")])]})});
            var Q10;
            Q10=makeQuery(id+"F3.boolean.opBoolean","COPY",EDGE,{"derivedFrom":makeQuery(id+"F3.opExtrude","SWEPT_EDGE",EDGE,{"disambiguationData":[OSD([sQuery(id+"F2.wireOp",EDGE,"E53"),sQuery(id+"F2.wireOp",EDGE,"E54")])]})});
            var Q11;
            Q11=makeQuery(id+"F3.boolean.opBoolean","COPY",EDGE,{"derivedFrom":makeQuery(id+"F3.opExtrude","SWEPT_EDGE",EDGE,{"disambiguationData":[OSD([sQuery(id+"F2.wireOp",EDGE,"E39.left"),sQuery(id+"F2.wireOp",EDGE,"E52")])]})});
            var Q12;
            {var subQ0=sQuery(id+"F4.wireOp",EDGE,"JNPfFNKI-4dOs-uEMB-4dgi-pzYB1QdObrBG");var subQ1=sQuery(id+"F4.wireOp",EDGE,"wLb6ngMH-sIbR-5BM4-EAh9-717Bkj5mp9Vk");Q12=makeQuery(id+"F7.boolean.opBoolean","COPY",EDGE,{"derivedFrom":makeQuery(id+"F7.opExtrude","SWEPT_EDGE",EDGE,{"disambiguationData":[OSD([subQ1,subQ0]),TDD([makeQuery(id+"F4.imprint","INTERSECT",VERTEX,{"disambiguationData":[OD(0.0)],"derivedFrom":[subQ1,subQ0]})])]})});}
            var Q13;
            {var subQ0=sQuery(id+"F4.wireOp",EDGE,"2x0Gxuwi-EWEO-aNM3-p2HO-Z3Mz9g2t8XBh");var subQ1=sQuery(id+"F4.wireOp",EDGE,"BXIdj9v8-HcG3-0t2C-wqnp-Gxui9m4bDAGf");Q13=makeQuery(id+"F7.boolean.opBoolean","COPY",EDGE,{"derivedFrom":makeQuery(id+"F7.opExtrude","SWEPT_EDGE",EDGE,{"disambiguationData":[OSD([subQ1,subQ0]),TDD([makeQuery(id+"F4.imprint","INTERSECT",VERTEX,{"disambiguationData":[OD(0.0)],"derivedFrom":[subQ1,subQ0]})])]})});}
            var Q14;
            {var subQ0=sQuery(id+"F4.wireOp",EDGE,"2x0Gxuwi-EWEO-aNM3-p2HO-Z3Mz9g2t8XBh");var subQ1=sQuery(id+"F4.wireOp",EDGE,"BXIdj9v8-HcG3-0t2C-wqnp-Gxui9m4bDAGf");Q14=makeQuery(id+"F7.boolean.opBoolean","COPY",EDGE,{"derivedFrom":makeQuery(id+"F7.opExtrude","SWEPT_EDGE",EDGE,{"disambiguationData":[OSD([subQ1,subQ0]),TDD([makeQuery(id+"F4.imprint","INTERSECT",VERTEX,{"disambiguationData":[OD(1.0)],"derivedFrom":[subQ1,subQ0]})])]})});}
            var Q15;
            {var subQ0=sQuery(id+"F4.wireOp",EDGE,"JNPfFNKI-4dOs-uEMB-4dgi-pzYB1QdObrBG");var subQ1=sQuery(id+"F4.wireOp",EDGE,"wLb6ngMH-sIbR-5BM4-EAh9-717Bkj5mp9Vk");Q15=makeQuery(id+"F7.boolean.opBoolean","COPY",EDGE,{"derivedFrom":makeQuery(id+"F7.opExtrude","SWEPT_EDGE",EDGE,{"disambiguationData":[OSD([subQ1,subQ0]),TDD([makeQuery(id+"F4.imprint","INTERSECT",VERTEX,{"disambiguationData":[OD(1.0)],"derivedFrom":[subQ1,subQ0]})])]})});}
            fillet(context, id + "F11", {"entities" : qUnion([Q0, Q1, Q2, Q3, Q4, Q5, Q6, Q7, Q8, Q9, Q10, Q11, Q12, Q13, Q14, Q15]), "radius" : 1 * mm, "tangentPropagation" : true, "allowEdgeOverflow" : false});
        }
    });
